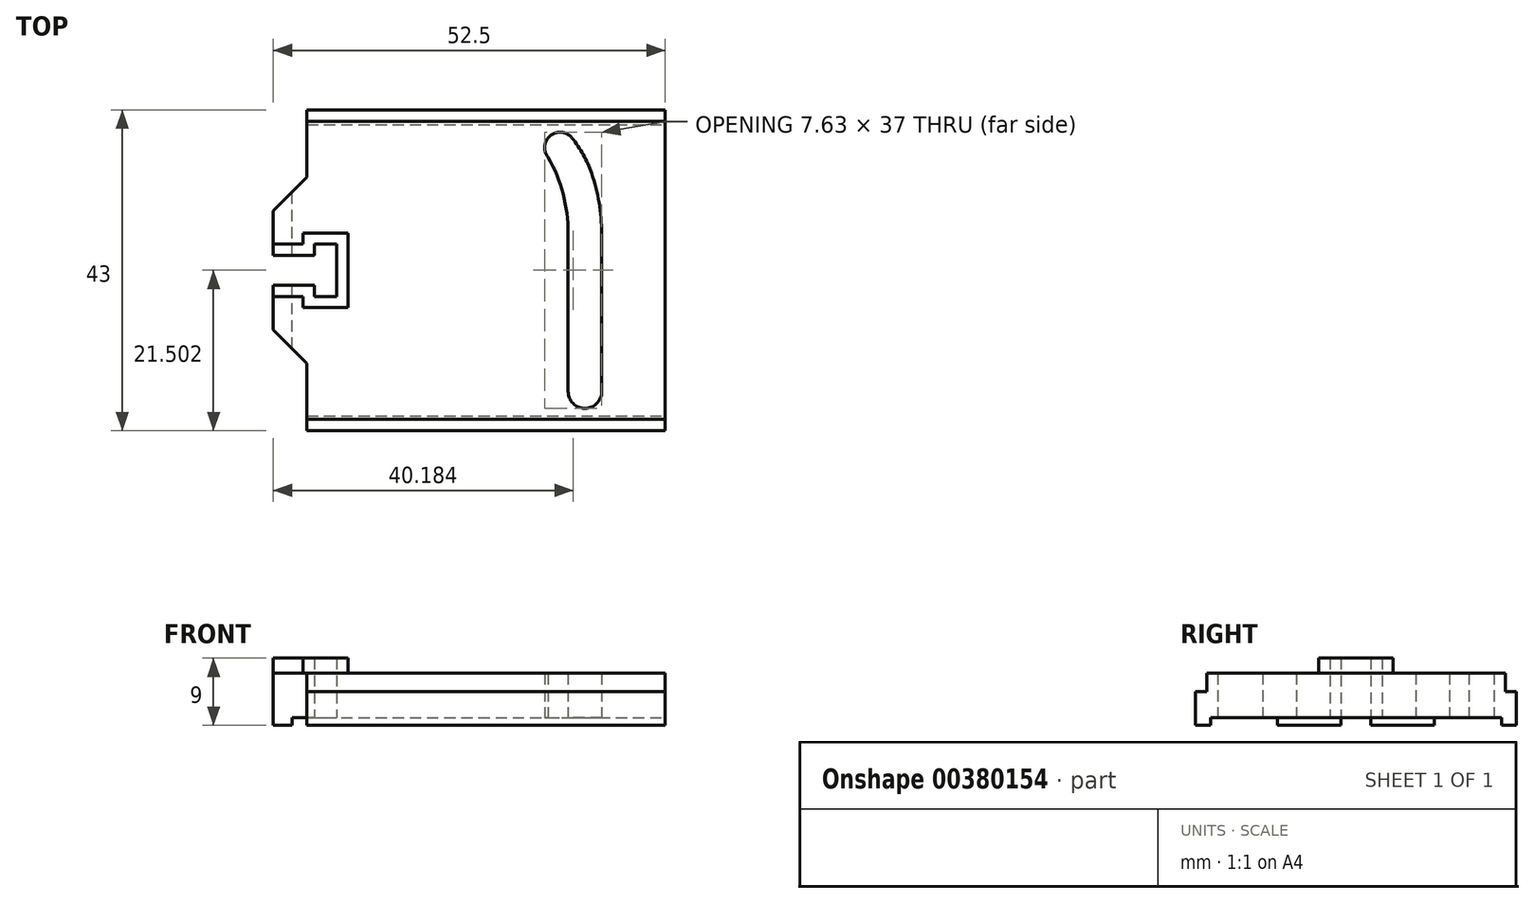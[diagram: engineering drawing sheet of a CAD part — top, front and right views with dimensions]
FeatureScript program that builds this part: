
annotation { "Feature Type Name" : "Feature", "Feature Type Description" : "" }
export const myFeature = defineFeature(function(context is Context, id is Id, definition is map)
    precondition{}
    {
        {
            var Q0;
            Q0=qCreatedBy(makeId("Top.planeOp"),FACE);
            var sketch = newSketch(context, id + "F0", { "sketchPlane" : qUnion([Q0])});
            skLineSegment(sketch, "E0.bottom", {"start": v(28.5, -21.5) * mm, "end": v(-19.5, -21.5) * mm});
            skLineSegment(sketch, "E0.top", {"start": v(28.5, 21.5) * mm, "end": v(-19.5, 21.5) * mm});
            skLineSegment(sketch, "E0.left", {"start": v(28.5, -21.5) * mm, "end": v(28.5, 21.5) * mm});
            skLineSegment(sketch, "E0.right", {"start": v(-24, -8) * mm, "end": v(-24, -2) * mm});
            skPoint(sketch, "E0.middle", {"position": v(0, 0) * mm});
            skLineSegment(sketch, "E1.left", {"start": v(-24, 8) * mm, "end": v(-24, 2) * mm});
            skLineSegment(sketch, "E1.right", {"start": v(-19.5, 21.5) * mm, "end": v(-19.5, 12.5) * mm});
            skLineSegment(sketch, "E2", {"start": v(-24, -8) * mm, "end": v(-19.5, -12.5) * mm});
            skLineSegment(sketch, "E3", {"start": v(-24, 8) * mm, "end": v(-19.5, 12.5) * mm});
            skLineSegment(sketch, "E4.trimOffspring", {"start": v(-19.5, -12.5) * mm, "end": v(-19.5, -21.5) * mm});
            skLineSegment(sketch, "E5.bottom", {"start": v(-24, 2) * mm, "end": v(-18.5, 2) * mm});
            skLineSegment(sketch, "E5.top", {"start": v(-24, -2) * mm, "end": v(-18.5, -2) * mm});
            skLineSegment(sketch, "E5.right", {"start": v(-15.5, 2) * mm, "end": v(-15.5, -2) * mm});
            skLineSegment(sketch, "E6.trimOffspring", {"start": v(-24, -2) * mm, "end": v(-24, -8) * mm});
            skLineSegment(sketch, "E7.trimOffspring", {"start": v(-24, 2) * mm, "end": v(-24, 8) * mm});
            skLineSegment(sketch, "E8", {"start": v(-15.5, 0) * mm, "end": v(-15.5, 3.5) * mm});
            skLineSegment(sketch, "E9", {"start": v(-15.5, 3.5) * mm, "end": v(-18.5, 3.5) * mm});
            skLineSegment(sketch, "E10", {"start": v(-18.5, 3.5) * mm, "end": v(-18.5, 2) * mm});
            skLineSegment(sketch, "E11", {"start": v(-15.5, 0) * mm, "end": v(-15.5, -3.5) * mm});
            skLineSegment(sketch, "E12", {"start": v(-15.5, -3.5) * mm, "end": v(-18.5, -3.5) * mm});
            skLineSegment(sketch, "E13", {"start": v(-18.5, -2) * mm, "end": v(-18.5, -3.5) * mm});
            skLineSegment(sketch, "E14.left", {"start": v(20, -14) * mm, "end": v(20, 5) * mm});
            skLineSegment(sketch, "E14.right", {"start": v(15.5, -14) * mm, "end": v(15.5, 5) * mm});
            skArc(sketch, "E15", {"start": v(15.5, 5) * mm, "mid": v(14.82, 10.24) * mm, "end": v(12.84, 15.14) * mm});
            skLineSegment(sketch, "E16.left", {"start": v(15.5, -16.25) * mm, "end": v(15.5, -14) * mm});
            skLineSegment(sketch, "E16.right", {"start": v(20, -16.25) * mm, "end": v(20, -14) * mm});
            skArc(sketch, "E17", {"start": v(15.5, -16.25) * mm, "mid": v(17.75, -18.5) * mm, "end": v(20, -16.25) * mm});
            skArc(sketch, "E18", {"start": v(16.01, 17.75) * mm, "mid": v(13.1, 18.04) * mm, "end": v(12.84, 15.14) * mm});
            skArc(sketch, "E19", {"start": v(20, 5) * mm, "mid": v(19.66, 9.07) * mm, "end": v(18.64, 13.03) * mm});
            skArc(sketch, "E20", {"start": v(18.64, 13.03) * mm, "mid": v(17.53, 15.5) * mm, "end": v(16.01, 17.75) * mm});
            skSolve(sketch);
        }
        {
            var Q0;
            Q0=makeQuery(id+"F0.imprint","IMPRINT",FACE,{"disambiguationData":[TD([[makeQuery(id+"F0.imprint","IMPRINT",EDGE,{"derivedFrom":sQuery(id+"F0.wireOp",EDGE,"E0.bottom")}),-1.0]])]});
            extrude(context, id + "F1", {"entities" : qUnion([Q0]), "depth" : 7 * mm});
        }
        {
            var Q0;
            Q0=makeQuery(id+"F1.opExtrude","SWEPT_FACE",FACE,{"disambiguationData":[OSD([sQuery(id+"F0.wireOp",EDGE,"E0.left")])]});
            var sketch = newSketch(context, id + "F2", { "sketchPlane" : qUnion([Q0])});
            skPoint(sketch, "E21", {"position": v(-19.5, 0) * mm});
            skPoint(sketch, "E22", {"position": v(19.5, 0) * mm});
            skLineSegment(sketch, "E23.bottom", {"start": v(-19.5, 0) * mm, "end": v(19.5, 0) * mm});
            skLineSegment(sketch, "E23.top", {"start": v(-19.5, 1) * mm, "end": v(19.5, 1) * mm});
            skLineSegment(sketch, "E23.left", {"start": v(-19.5, 0) * mm, "end": v(-19.5, 1) * mm});
            skLineSegment(sketch, "E23.right", {"start": v(19.5, 0) * mm, "end": v(19.5, 1) * mm});
            skSolve(sketch);
        }
        {
            var Q0;
            Q0=makeQuery(id+"F2.imprint","IMPRINT",FACE,{"disambiguationData":[TD([[makeQuery(id+"F2.imprint","IMPRINT",EDGE,{"derivedFrom":sQuery(id+"F2.wireOp",EDGE,"E23.bottom")}),1.0]])]});
            extrude(context, id + "F3", {"entities" : qUnion([Q0]), "operationType" : NewBodyOperationType.REMOVE, "oppositeDirection" : true, "depth" : 50 * mm});
        }
        {
            var Q0;
            Q0=makeQuery(id+"F1.opExtrude","CAP_FACE",FACE,{"disambiguationData":[OSD([sQuery(id+"F0.wireOp",EDGE,"E0.bottom"),sQuery(id+"F0.wireOp",EDGE,"E0.top"),sQuery(id+"F0.wireOp",EDGE,"E0.left"),sQuery(id+"F0.wireOp",EDGE,"E1.right"),sQuery(id+"F0.wireOp",EDGE,"E2"),sQuery(id+"F0.wireOp",EDGE,"E3"),sQuery(id+"F0.wireOp",EDGE,"E4.trimOffspring"),sQuery(id+"F0.wireOp",EDGE,"E5.bottom"),sQuery(id+"F0.wireOp",EDGE,"E5.top"),sQuery(id+"F0.wireOp",EDGE,"E6.trimOffspring"),sQuery(id+"F0.wireOp",EDGE,"E7.trimOffspring"),sQuery(id+"F0.wireOp",EDGE,"E8"),sQuery(id+"F0.wireOp",EDGE,"E9"),sQuery(id+"F0.wireOp",EDGE,"E10"),sQuery(id+"F0.wireOp",EDGE,"E11"),sQuery(id+"F0.wireOp",EDGE,"E12"),sQuery(id+"F0.wireOp",EDGE,"E13"),sQuery(id+"F0.wireOp",EDGE,"E14.left"),sQuery(id+"F0.wireOp",EDGE,"E14.right"),sQuery(id+"F0.wireOp",EDGE,"E15"),sQuery(id+"F0.wireOp",EDGE,"E16.left"),sQuery(id+"F0.wireOp",EDGE,"E16.right"),sQuery(id+"F0.wireOp",EDGE,"E17"),sQuery(id+"F0.wireOp",EDGE,"E18"),sQuery(id+"F0.wireOp",EDGE,"E19"),sQuery(id+"F0.wireOp",EDGE,"E20")])],"isStart":false});
            var sketch = newSketch(context, id + "F4", { "sketchPlane" : qUnion([Q0])});
            skPoint(sketch, "E24", {"position": v(-14, 5) * mm});
            skPoint(sketch, "E25", {"position": v(-20, 5) * mm});
            skPoint(sketch, "E26", {"position": v(-20, 3.5) * mm});
            skPoint(sketch, "E27", {"position": v(-24, 3.5) * mm});
            skPoint(sketch, "E28", {"position": v(-24, -3.5) * mm});
            skPoint(sketch, "E29", {"position": v(-20, -3.5) * mm});
            skPoint(sketch, "E30", {"position": v(-20, -5) * mm});
            skPoint(sketch, "E31", {"position": v(-14, -5) * mm});
            skLineSegment(sketch, "E32", {"start": v(-24, -3.5) * mm, "end": v(-20, -3.5) * mm});
            skLineSegment(sketch, "E33", {"start": v(-20, -5) * mm, "end": v(-14, -5) * mm});
            skLineSegment(sketch, "E34", {"start": v(-14, 5) * mm, "end": v(-14, -5) * mm});
            skLineSegment(sketch, "E35", {"start": v(-14, 5) * mm, "end": v(-20, 5) * mm});
            skLineSegment(sketch, "E36", {"start": v(-20, 5) * mm, "end": v(-20, 3.5) * mm});
            skLineSegment(sketch, "E37", {"start": v(-20, 3.5) * mm, "end": v(-24, 3.5) * mm});
            skLineSegment(sketch, "E38", {"start": v(-20, -3.5) * mm, "end": v(-20, -5) * mm});
            skSolve(sketch);
        }
        {
            var Q0;
            {var subQ2=sQuery(id+"F4.wireOp",EDGE,"E32");Q0=makeQuery(id+"F4.imprint","IMPRINT",FACE,{"disambiguationData":[TD([[makeQuery(id+"F4.imprint","IMPRINT",EDGE,{"derivedFrom":subQ2}),1.0]])]});}
            extrude(context, id + "F5", {"entities" : qUnion([Q0]), "operationType" : NewBodyOperationType.ADD, "depth" : 2 * mm});
        }
        {
            var Q0;
            Q0=makeQuery(id+"F1.opExtrude","SWEPT_FACE",FACE,{"disambiguationData":[OSD([sQuery(id+"F0.wireOp",EDGE,"E0.left")])]});
            var sketch = newSketch(context, id + "F6", { "sketchPlane" : qUnion([Q0])});
            skLineSegment(sketch, "E39.bottom", {"start": v(20, 7) * mm, "end": v(21.5, 7) * mm});
            skLineSegment(sketch, "E39.top", {"start": v(20, 4.5) * mm, "end": v(21.5, 4.5) * mm});
            skLineSegment(sketch, "E39.left", {"start": v(20, 7) * mm, "end": v(20, 4.5) * mm});
            skLineSegment(sketch, "E39.right", {"start": v(21.5, 7) * mm, "end": v(21.5, 4.5) * mm});
            skLineSegment(sketch, "E40.bottom", {"start": v(-21.5, 7) * mm, "end": v(-20, 7) * mm});
            skLineSegment(sketch, "E40.top", {"start": v(-21.5, 4.5) * mm, "end": v(-20, 4.5) * mm});
            skLineSegment(sketch, "E40.left", {"start": v(-21.5, 7) * mm, "end": v(-21.5, 4.5) * mm});
            skLineSegment(sketch, "E40.right", {"start": v(-20, 7) * mm, "end": v(-20, 4.5) * mm});
            skSolve(sketch);
        }
        {
            var Q0;
            Q0=makeQuery(id+"F6.imprint","IMPRINT",FACE,{"disambiguationData":[TD([[makeQuery(id+"F6.imprint","IMPRINT",EDGE,{"derivedFrom":sQuery(id+"F6.wireOp",EDGE,"E40.bottom")}),-1.0]])]});
            var Q1;
            Q1=makeQuery(id+"F6.imprint","IMPRINT",FACE,{"disambiguationData":[TD([[makeQuery(id+"F6.imprint","IMPRINT",EDGE,{"derivedFrom":sQuery(id+"F6.wireOp",EDGE,"E39.bottom")}),-1.0]])]});
            extrude(context, id + "F7", {"entities" : qUnion([Q0, Q1]), "operationType" : NewBodyOperationType.REMOVE, "oppositeDirection" : true, "depth" : 50 * mm});
        }
    });
